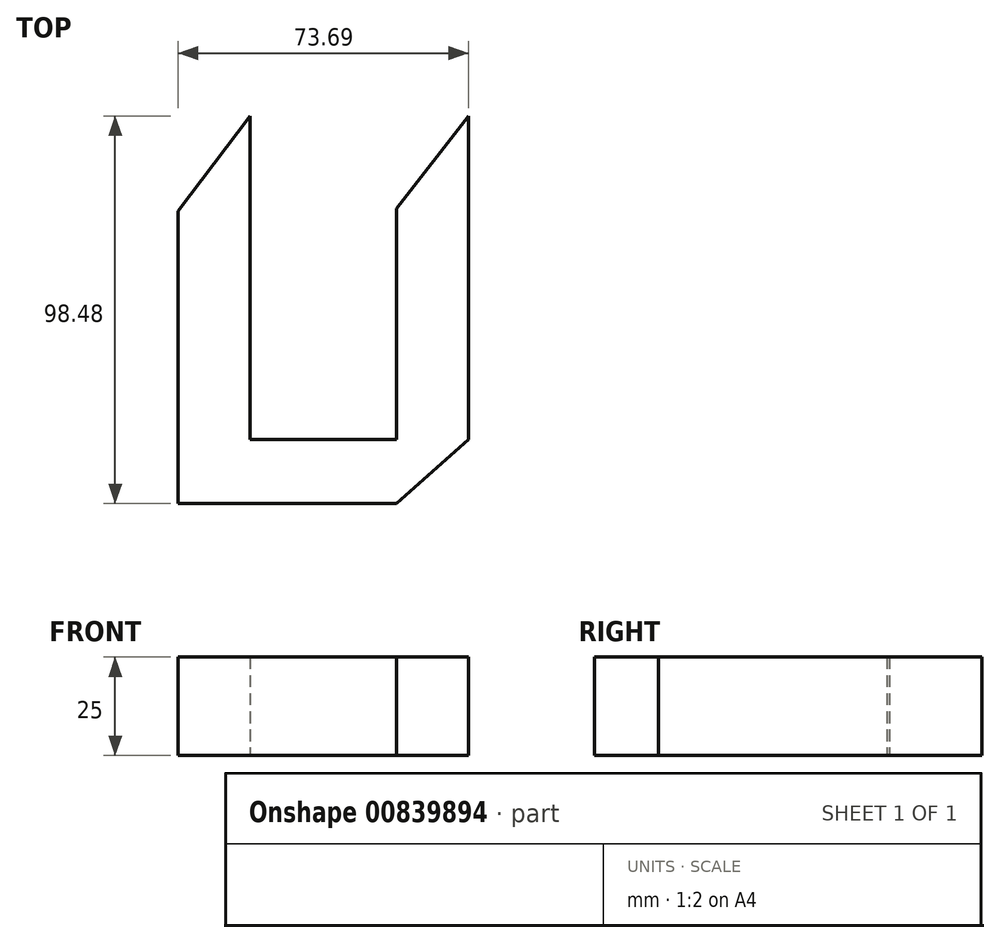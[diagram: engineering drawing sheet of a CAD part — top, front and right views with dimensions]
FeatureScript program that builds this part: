
annotation { "Feature Type Name" : "Feature", "Feature Type Description" : "" }
export const myFeature = defineFeature(function(context is Context, id is Id, definition is map)
    precondition{}
    {
        {
            var Q0;
            Q0=qCreatedBy(makeId("Top.planeOp"),FACE);
            var sketch = newSketch(context, id + "F0", { "sketchPlane" : qUnion([Q0])});
            skLineSegment(sketch, "E0", {"start": v(-25.6, 43.7) * mm, "end": v(27.55, 43.7) * mm});
            skLineSegment(sketch, "E1", {"start": v(27.55, 43.7) * mm, "end": v(27.55, 0) * mm});
            skLineSegment(sketch, "E2", {"start": v(27.55, 0) * mm, "end": v(27.55, -38.48) * mm});
            skLineSegment(sketch, "E3", {"start": v(27.55, -38.48) * mm, "end": v(-27.88, -38.48) * mm});
            skLineSegment(sketch, "E4", {"start": v(-27.88, -38.48) * mm, "end": v(-27.88, 43.7) * mm});
            skLineSegment(sketch, "E5", {"start": v(-27.88, 43.7) * mm, "end": v(-25.6, 43.7) * mm});
            skLineSegment(sketch, "E6", {"start": v(-27.88, 43.7) * mm, "end": v(-46.14, 19.57) * mm});
            skLineSegment(sketch, "E7", {"start": v(-46.14, 19.57) * mm, "end": v(-46.14, -54.78) * mm});
            skLineSegment(sketch, "E8", {"start": v(-46.14, -54.78) * mm, "end": v(-27.88, -38.48) * mm});
            skLineSegment(sketch, "E9", {"start": v(27.55, 43.7) * mm, "end": v(9.3, 20.22) * mm});
            skLineSegment(sketch, "E10", {"start": v(9.3, 20.22) * mm, "end": v(9.3, -54.78) * mm});
            skLineSegment(sketch, "E11", {"start": v(9.3, -54.78) * mm, "end": v(27.55, -38.48) * mm});
            skLineSegment(sketch, "E12", {"start": v(-46.14, 19.57) * mm, "end": v(9.3, 20.22) * mm});
            skLineSegment(sketch, "E13", {"start": v(-46.14, -54.78) * mm, "end": v(9.3, -54.78) * mm});
            skSolve(sketch);
        }
        {
            var Q0;
            {var subQ0=sQuery(id+"F0.wireOp",EDGE,"E11");Q0=makeQuery(id+"F0.imprint","IMPRINT",FACE,{"disambiguationData":[TD([[makeQuery(id+"F0.imprint","IMPRINT",EDGE,{"derivedFrom":subQ0}),1.0]])]});}
            var Q1;
            {var subQ0=sQuery(id+"F0.wireOp",EDGE,"E6");Q1=makeQuery(id+"F0.imprint","IMPRINT",FACE,{"disambiguationData":[TD([[makeQuery(id+"F0.imprint","IMPRINT",EDGE,{"derivedFrom":subQ0}),1.0]])]});}
            var Q2;
            Q2=makeQuery(id+"F0.imprint","IMPRINT",FACE,{"disambiguationData":[TD([[makeQuery(id+"F0.imprint","IMPRINT",EDGE,{"derivedFrom":sQuery(id+"F0.wireOp",EDGE,"E1")}),-1.0]])]});
            var Q3;
            {var subQ0=sQuery(id+"F0.wireOp",EDGE,"E8");Q3=makeQuery(id+"F0.imprint","IMPRINT",FACE,{"disambiguationData":[TD([[makeQuery(id+"F0.imprint","IMPRINT",EDGE,{"derivedFrom":subQ0}),-1.0]])]});}
            var Q4;
            {var subQ4=sQuery(id+"F0.wireOp",EDGE,"E7");Q4=makeQuery(id+"F0.imprint","IMPRINT",FACE,{"disambiguationData":[TD([[makeQuery(id+"F0.imprint","IMPRINT",EDGE,{"derivedFrom":subQ4}),1.0]])]});}
            extrude(context, id + "F1", {"entities" : qUnion([Q0, Q1, Q2, Q3, Q4]), "depth" : 25 * mm, "offsetDistance" : 25 * mm});
        }
    });
